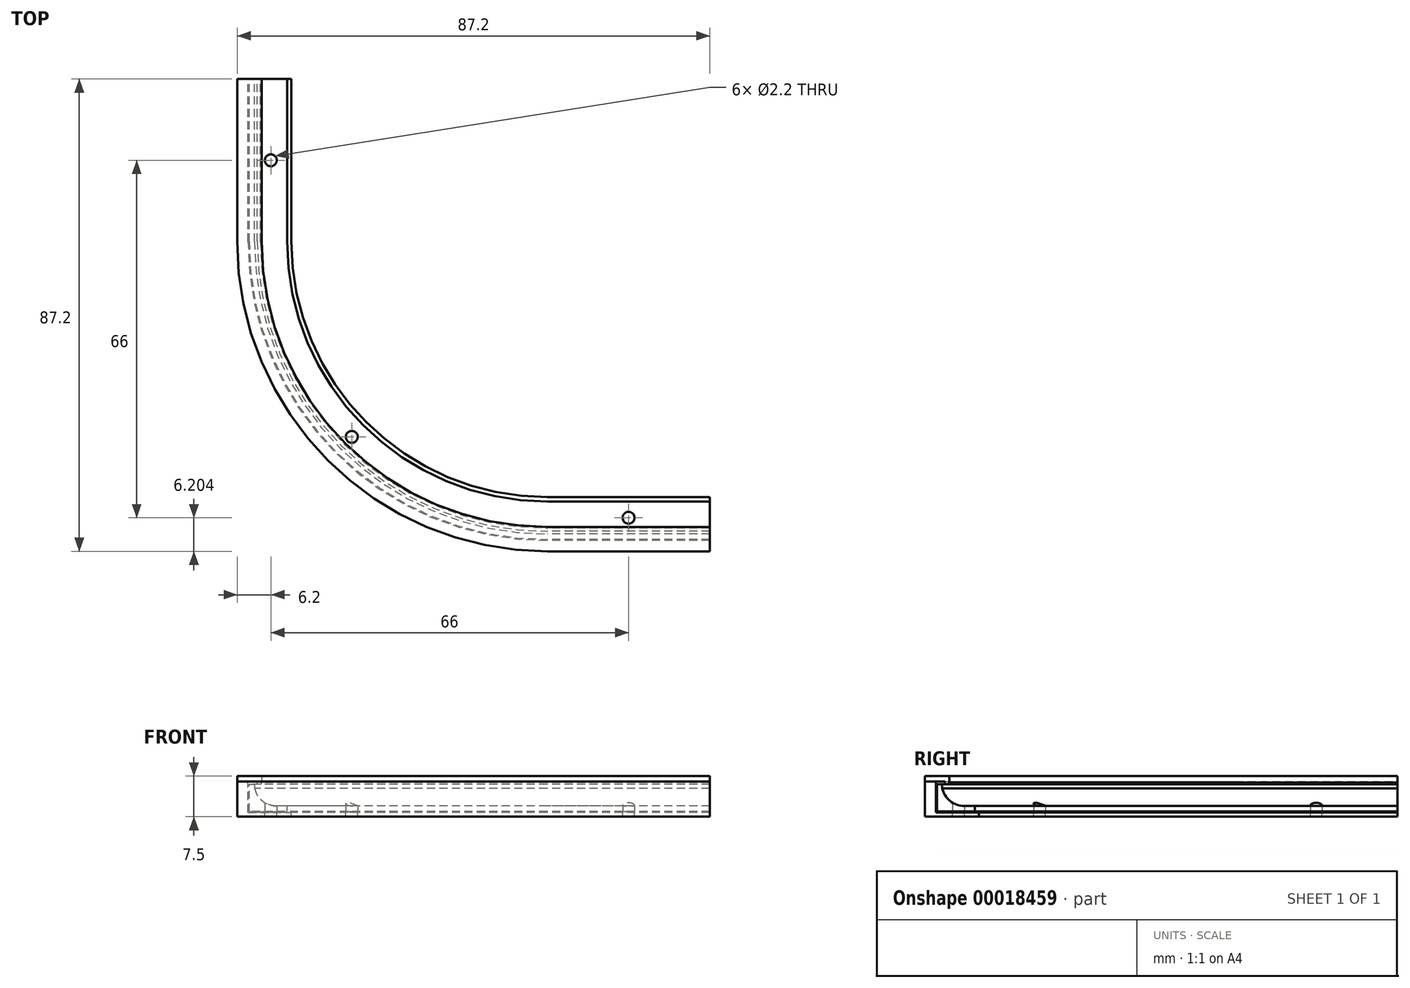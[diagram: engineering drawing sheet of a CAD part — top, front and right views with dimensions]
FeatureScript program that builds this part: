
annotation { "Feature Type Name" : "Feature", "Feature Type Description" : "" }
export const myFeature = defineFeature(function(context is Context, id is Id, definition is map)
    precondition{}
    {
        {
            var Q0;
            Q0=qCreatedBy(makeId("Top.planeOp"),FACE);
            var sketch = newSketch(context, id + "F0", { "sketchPlane" : qUnion([Q0])});
            skLineSegment(sketch, "E0", {"start": v(-80, 28.54) * mm, "end": v(-80, -1.46) * mm});
            skLineSegment(sketch, "E1", {"start": v(-30, -51.46) * mm, "end": v(0, -51.46) * mm});
            skPoint(sketch, "E2.visualSharp", {"position": v(-80, -51.46) * mm});
            skArc(sketch, "E2.filletArc", {"start": v(-80, -1.46) * mm, "mid": v(-65.36, -36.81) * mm, "end": v(-30, -51.46) * mm});
            skLineSegment(sketch, "E3.0", {"start": v(-30, -52.46) * mm, "end": v(0, -52.46) * mm, "construction": true});
            skArc(sketch, "E3.1", {"start": v(-81, -1.46) * mm, "mid": v(-66.06, -37.52) * mm, "end": v(-30, -52.46) * mm, "construction": true});
            skLineSegment(sketch, "E3.2", {"start": v(-81, 28.54) * mm, "end": v(-81, -1.46) * mm, "construction": true});
            skLineSegment(sketch, "E4", {"start": v(-66.06, -37.52) * mm, "end": v(-30, -1.46) * mm, "construction": true});
            skLineSegment(sketch, "E5", {"start": v(-81, 13.54) * mm, "end": v(-60.53, 13.54) * mm, "construction": true});
            skLineSegment(sketch, "E6", {"start": v(-15, -52.46) * mm, "end": v(-15, -33.12) * mm, "construction": true});
            skSolve(sketch);
        }
        {
            var Q0;
            Q0=qCreatedBy(makeId("Right.planeOp"),FACE);
            var sketch = newSketch(context, id + "F1", { "sketchPlane" : qUnion([Q0])});
            skLineSegment(sketch, "E7", {"start": v(-56.46, 0) * mm, "end": v(-56.46, 5) * mm});
            skLineSegment(sketch, "E8", {"start": v(-56.46, 5) * mm, "end": v(-55.46, 5) * mm});
            skLineSegment(sketch, "E9", {"start": v(-58.66, -1) * mm, "end": v(-48.66, -1) * mm});
            skLineSegment(sketch, "E10", {"start": v(-48.66, -1) * mm, "end": v(-48.66, -0.2) * mm});
            skLineSegment(sketch, "E11", {"start": v(-56.66, -0.2) * mm, "end": v(-48.66, -0.2) * mm});
            skPoint(sketch, "E12.orphan", {"position": v(-48.66, 0) * mm});
            skLineSegment(sketch, "E13", {"start": v(-54.37, 5) * mm, "end": v(-54.96, 5) * mm});
            skLineSegment(sketch, "E14", {"start": v(-54.96, 5) * mm, "end": v(-54.96, 5.5) * mm});
            skLineSegment(sketch, "E15", {"start": v(-54.16, 5.3) * mm, "end": v(-54.37, 5) * mm});
            skLineSegment(sketch, "E16", {"start": v(-54.96, 5.5) * mm, "end": v(-58.66, 5.5) * mm});
            skLineSegment(sketch, "E17", {"start": v(-58.66, 6.5) * mm, "end": v(-54.16, 6.5) * mm});
            skLineSegment(sketch, "E18", {"start": v(-54.16, 6.5) * mm, "end": v(-54.16, 5.3) * mm});
            skLineSegment(sketch, "E19", {"start": v(-58.66, -1) * mm, "end": v(-58.66, 5.5) * mm});
            skLineSegment(sketch, "E20", {"start": v(-56.66, -0.2) * mm, "end": v(-56.66, 5.5) * mm});
            skLineSegment(sketch, "E21", {"start": v(-56.66, 5.5) * mm, "end": v(-58.66, 5.5) * mm});
            skLineSegment(sketch, "E22", {"start": v(-49.46, 0) * mm, "end": v(-49.46, 1) * mm});
            skPoint(sketch, "E23.start.orphan", {"position": v(-51.46, 0) * mm});
            skLineSegment(sketch, "E24", {"start": v(-56.46, 0) * mm, "end": v(-49.46, 0) * mm});
            skLineSegment(sketch, "E25", {"start": v(-49.46, 1) * mm, "end": v(-51.46, 1) * mm});
            skLineSegment(sketch, "E26", {"start": v(-55.46, 5) * mm, "end": v(-55.46, 4.24) * mm});
            skArc(sketch, "E27", {"start": v(-55.46, 4.24) * mm, "mid": v(-54.03, 1.91) * mm, "end": v(-51.46, 1) * mm});
            skLineSegment(sketch, "E28", {"start": v(-58.66, 5.5) * mm, "end": v(-58.66, 6.5) * mm});
            skSolve(sketch);
        }
        {
            var Q0;
            Q0=makeQuery(id+"F1.imprint","IMPRINT",FACE,{"disambiguationData":[TD([[makeQuery(id+"F1.imprint","IMPRINT",EDGE,{"derivedFrom":sQuery(id+"F1.wireOp",EDGE,"E7")}),-1.0]])]});
            var Q1;
            Q1=sQuery(id+"F0.wireOp",EDGE,"E1");
            var Q2;
            Q2=sQuery(id+"F0.wireOp",EDGE,"E2.filletArc");
            var Q3;
            Q3=sQuery(id+"F0.wireOp",EDGE,"E0");
            sweep(context, id + "F2", {"profiles" : qUnion([Q0]), "path" : qUnion([Q1, Q2, Q3])});
        }
        {
            var Q0;
            Q0=makeQuery(id+"F1.imprint","IMPRINT",FACE,{"disambiguationData":[TD([[makeQuery(id+"F1.imprint","IMPRINT",EDGE,{"derivedFrom":sQuery(id+"F1.wireOp",EDGE,"E9")}),1.0]])]});
            var Q1;
            Q1 = qConstructionFilter(qBodyType(qCreatedBy(id + "F0" ,EDGE), BodyType.WIRE), ConstructionObject.NO);
            sweep(context, id + "F3", {"profiles" : qUnion([Q0]), "path" : qUnion([Q1])});
        }
        {
            var Q0;
            Q0=makeQuery(id+"F1.imprint","IMPRINT",FACE,{"disambiguationData":[TD([[makeQuery(id+"F1.imprint","IMPRINT",EDGE,{"derivedFrom":sQuery(id+"F1.wireOp",EDGE,"E13")}),-1.0]])]});
            var Q1;
            Q1 = qConstructionFilter(qBodyType(qCreatedBy(id + "F0" ,EDGE), BodyType.WIRE), ConstructionObject.NO);
            sweep(context, id + "F4", {"profiles" : qUnion([Q0]), "path" : qUnion([Q1])});
        }
        {
            var Q0;
            Q0=sQuery(id+"F0.wireOp",VERTEX,"E5.start");
            var Q1;
            Q1=sQuery(id+"F0.wireOp",VERTEX,"E4.start");
            var Q2;
            Q2=sQuery(id+"F0.wireOp",VERTEX,"E6.start");
            var Q3;
            Q3=makeQuery(id+"F3.opSweep","SWEPT_BODY",BODY,{"disambiguationData":[OSD([sQuery(id+"F0.wireOp",EDGE,"E1"),sQuery(id+"F1.wireOp",EDGE,"E9"),sQuery(id+"F1.wireOp",EDGE,"E10"),sQuery(id+"F1.wireOp",EDGE,"E11"),sQuery(id+"F1.wireOp",EDGE,"E19"),sQuery(id+"F1.wireOp",EDGE,"E20"),sQuery(id+"F1.wireOp",EDGE,"E21")])]});
            var Q4;
            Q4=makeQuery(id+"F2.opSweep","SWEPT_BODY",BODY,{"disambiguationData":[OSD([sQuery(id+"F0.wireOp",EDGE,"E0"),sQuery(id+"F1.wireOp",EDGE,"E7"),sQuery(id+"F1.wireOp",EDGE,"E8"),sQuery(id+"F1.wireOp",EDGE,"E22"),sQuery(id+"F1.wireOp",EDGE,"E24"),sQuery(id+"F1.wireOp",EDGE,"E25"),sQuery(id+"F1.wireOp",EDGE,"E26"),sQuery(id+"F1.wireOp",EDGE,"E27")])]});
            hole(context, id + "F5", {"style" : HoleStyle.SIMPLE, "holeDiameter" : 2.2 * mm, "endStyle" : HoleEndStyle.THROUGH, "oppositeDirection" : true, "locations" : qUnion([Q0, Q1, Q2]), "scope" : qUnion([Q3, Q4])});
        }
        {
            var Q0;
            Q0=sQuery(id+"F0.wireOp",VERTEX,"E5.start");
            var Q1;
            Q1=sQuery(id+"F0.wireOp",VERTEX,"E4.start");
            var Q2;
            Q2=sQuery(id+"F0.wireOp",VERTEX,"E6.start");
            var Q3;
            Q3=makeQuery(id+"F3.opSweep","SWEPT_BODY",BODY,{"disambiguationData":[OSD([sQuery(id+"F0.wireOp",EDGE,"E1"),sQuery(id+"F1.wireOp",EDGE,"E9"),sQuery(id+"F1.wireOp",EDGE,"E10"),sQuery(id+"F1.wireOp",EDGE,"E11"),sQuery(id+"F1.wireOp",EDGE,"E19"),sQuery(id+"F1.wireOp",EDGE,"E20"),sQuery(id+"F1.wireOp",EDGE,"E21")])]});
            hole(context, id + "F6", {"style" : HoleStyle.SIMPLE, "holeDiameter" : 2.2 * mm, "endStyle" : HoleEndStyle.THROUGH, "locations" : qUnion([Q0, Q1, Q2]), "scope" : qUnion([Q3])});
        }
    });
